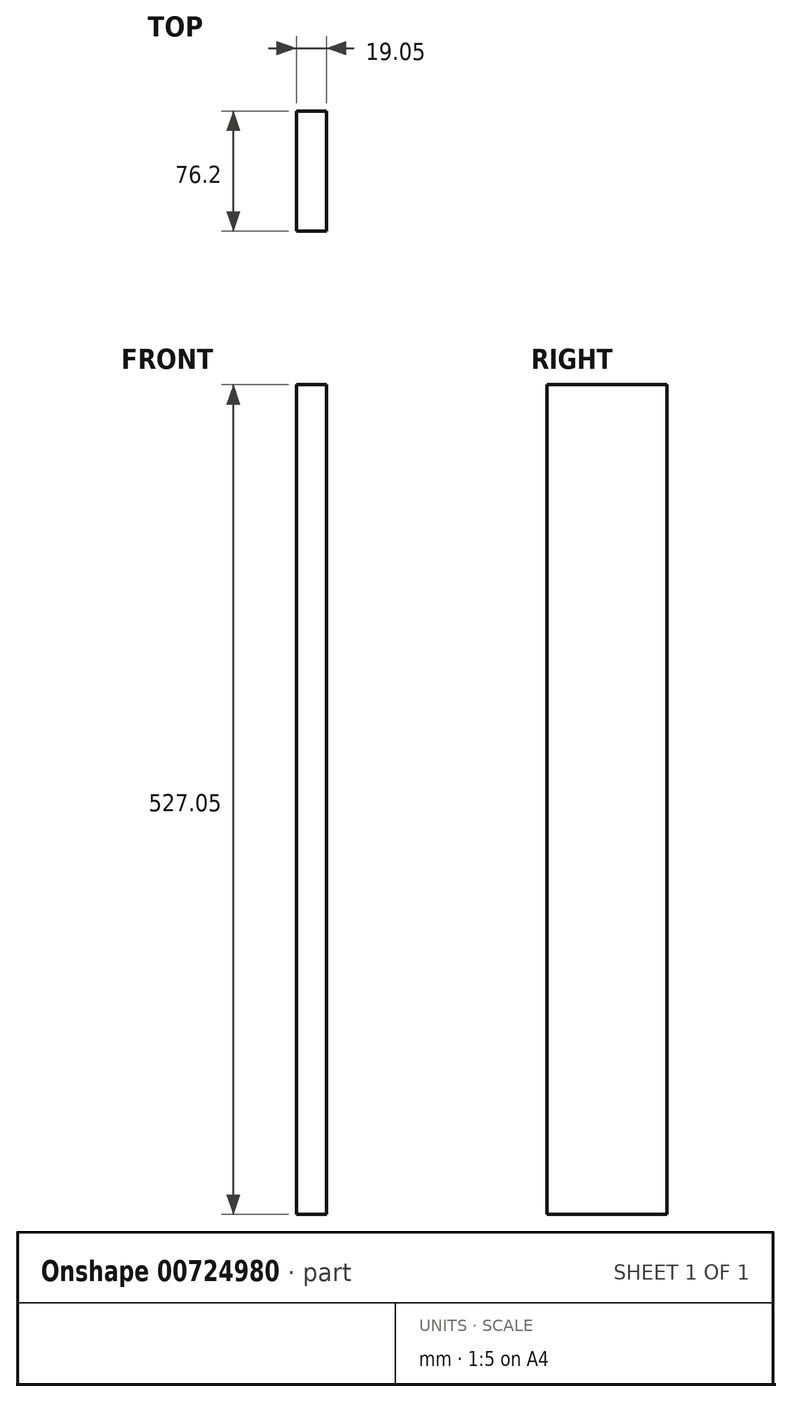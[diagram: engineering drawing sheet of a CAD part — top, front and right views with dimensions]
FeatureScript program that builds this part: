
annotation { "Feature Type Name" : "Feature", "Feature Type Description" : "" }
export const myFeature = defineFeature(function(context is Context, id is Id, definition is map)
    precondition{}
    {
        {
            var Q0;
            Q0=qCreatedBy(makeId("Top.planeOp"),FACE);
            var sketch = newSketch(context, id + "F0", { "sketchPlane" : qUnion([Q0])});
            skLineSegment(sketch, "E0.bottom", {"start": v(38.1, 38.1) * mm, "end": v(-38.1, 38.1) * mm});
            skLineSegment(sketch, "E0.top", {"start": v(38.1, -38.1) * mm, "end": v(-38.1, -38.1) * mm});
            skLineSegment(sketch, "E0.left", {"start": v(38.1, 38.1) * mm, "end": v(38.1, -38.1) * mm});
            skLineSegment(sketch, "E0.right", {"start": v(-38.1, 38.1) * mm, "end": v(-38.1, -38.1) * mm});
            skPoint(sketch, "E0.middle", {"position": v(0, 0) * mm});
            skLineSegment(sketch, "E1", {"start": v(-38.1, 38.1) * mm, "end": v(-19.05, 38.1) * mm});
            skLineSegment(sketch, "E2", {"start": v(-19.05, 38.1) * mm, "end": v(-19.05, -38.1) * mm});
            skLineSegment(sketch, "E3", {"start": v(38.1, -38.1) * mm, "end": v(38.1, -19.05) * mm});
            skLineSegment(sketch, "E4", {"start": v(38.1, -19.05) * mm, "end": v(-19.05, -19.05) * mm});
            skSolve(sketch);
        }
        {
            var Q0;
            {var subQ3=sQuery(id+"F0.wireOp",EDGE,"E0.right");Q0=makeQuery(id+"F0.imprint","IMPRINT",FACE,{"disambiguationData":[TD([[makeQuery(id+"F0.imprint","IMPRINT",EDGE,{"derivedFrom":subQ3}),1.0]])]});}
            var Q1;
            {var subQ0=sQuery(id+"F0.wireOp",EDGE,"E3");Q1=makeQuery(id+"F0.imprint","IMPRINT",FACE,{"disambiguationData":[TD([[makeQuery(id+"F0.imprint","IMPRINT",EDGE,{"derivedFrom":subQ0}),1.0]])]});}
            extrude(context, id + "F1", {"entities" : qUnion([Q0, Q1]), "depth" : 527.05 * mm, "offsetDistance" : 25.4 * mm});
        }
    });
